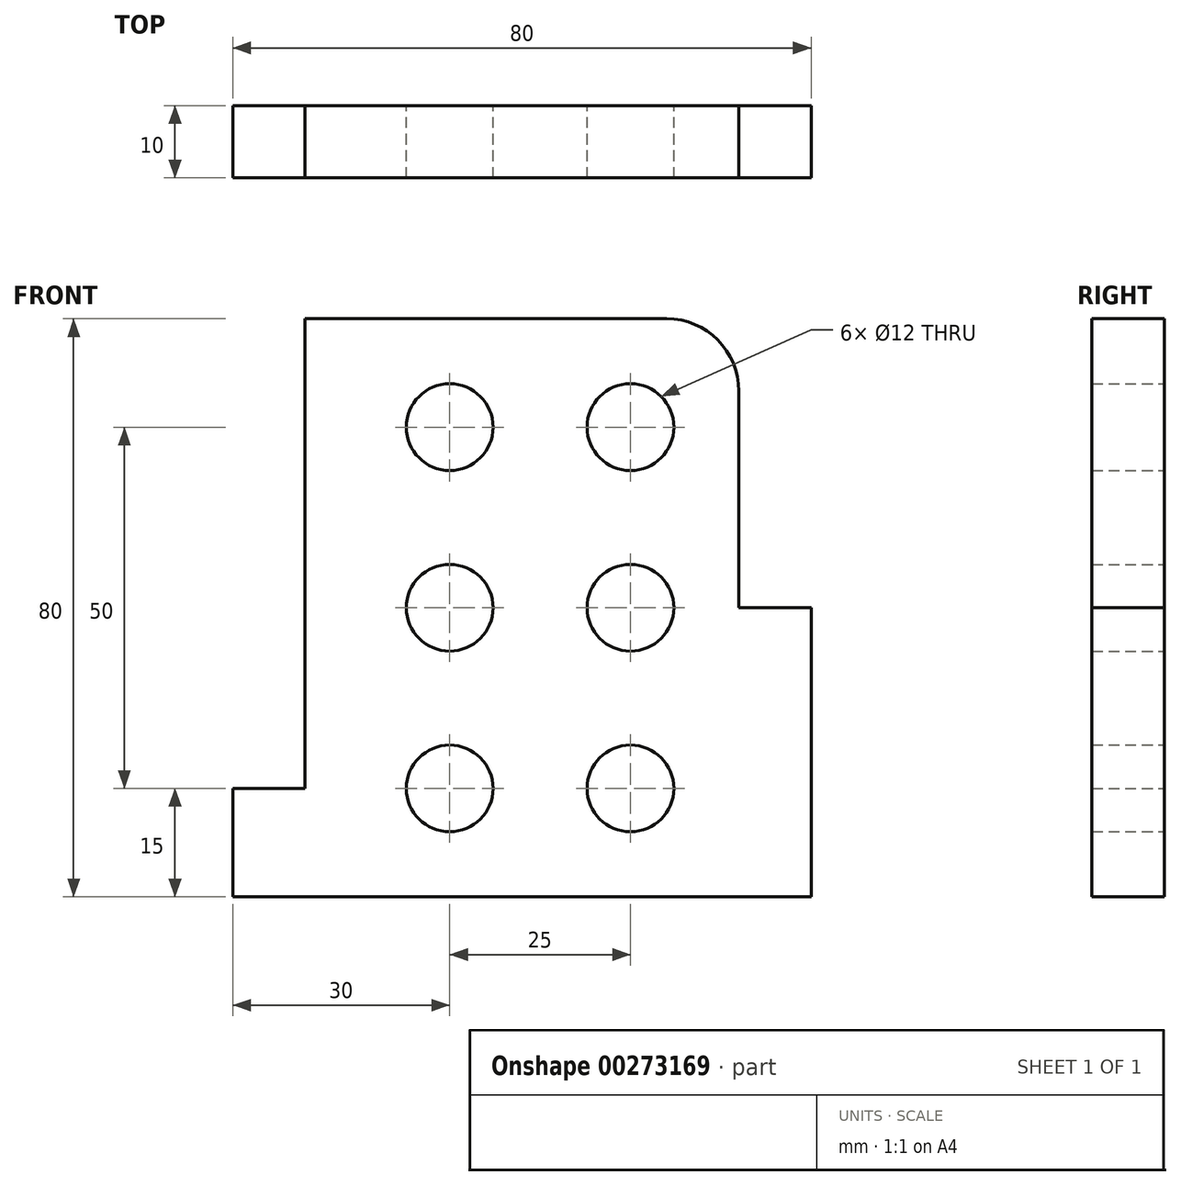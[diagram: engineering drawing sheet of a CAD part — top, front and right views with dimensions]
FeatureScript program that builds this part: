
annotation { "Feature Type Name" : "Feature", "Feature Type Description" : "" }
export const myFeature = defineFeature(function(context is Context, id is Id, definition is map)
    precondition{}
    {
        {
            var Q0;
            Q0=qCreatedBy(makeId("Front.planeOp"),FACE);
            var sketch = newSketch(context, id + "F0", { "sketchPlane" : qUnion([Q0])});
            skLineSegment(sketch, "E0", {"start": v(0, 0) * mm, "end": v(0, 15) * mm});
            skLineSegment(sketch, "E1", {"start": v(0, 15) * mm, "end": v(10, 15) * mm});
            skLineSegment(sketch, "E2", {"start": v(10, 15) * mm, "end": v(10, 80) * mm});
            skLineSegment(sketch, "E3", {"start": v(10, 80) * mm, "end": v(60, 80) * mm});
            skLineSegment(sketch, "E4", {"start": v(70, 70) * mm, "end": v(70, 40) * mm});
            skLineSegment(sketch, "E5", {"start": v(70, 40) * mm, "end": v(80, 40) * mm});
            skLineSegment(sketch, "E6", {"start": v(80, 40) * mm, "end": v(80, 0) * mm});
            skLineSegment(sketch, "E7", {"start": v(80, 0) * mm, "end": v(0, 0) * mm});
            skLineSegment(sketch, "E8", {"start": v(30, 67.28) * mm, "end": v(30, 10.2) * mm, "construction": true});
            skLineSegment(sketch, "E9", {"start": v(55, 67.28) * mm, "end": v(55, 10.2) * mm, "construction": true});
            skLineSegment(sketch, "E10", {"start": v(16.43, 65) * mm, "end": v(63.3, 65) * mm, "construction": true});
            skLineSegment(sketch, "E11", {"start": v(63.3, 40) * mm, "end": v(16.43, 40) * mm, "construction": true});
            skLineSegment(sketch, "E12", {"start": v(16.43, 15) * mm, "end": v(63.3, 15) * mm, "construction": true});
            skArc(sketch, "E13", {"start": v(70, 70) * mm, "mid": v(67.07, 77.07) * mm, "end": v(60, 80) * mm});
            skCircle(sketch, "E14", {"center": v(30, 65) * mm, "radius": 6 * mm});
            skCircle(sketch, "E15", {"center": v(30, 40) * mm, "radius": 6 * mm});
            skCircle(sketch, "E16", {"center": v(30, 15) * mm, "radius": 6 * mm});
            skCircle(sketch, "E17", {"center": v(55, 15) * mm, "radius": 6 * mm});
            skCircle(sketch, "E18", {"center": v(55, 40) * mm, "radius": 6 * mm});
            skCircle(sketch, "E19", {"center": v(55, 65) * mm, "radius": 6 * mm});
            skSolve(sketch);
        }
        {
            var Q0;
            Q0 = qSketchRegion(id + "F0", true);
            extrude(context, id + "F1", {"entities" : qUnion([Q0]), "depth" : 10 * mm});
        }
    });
